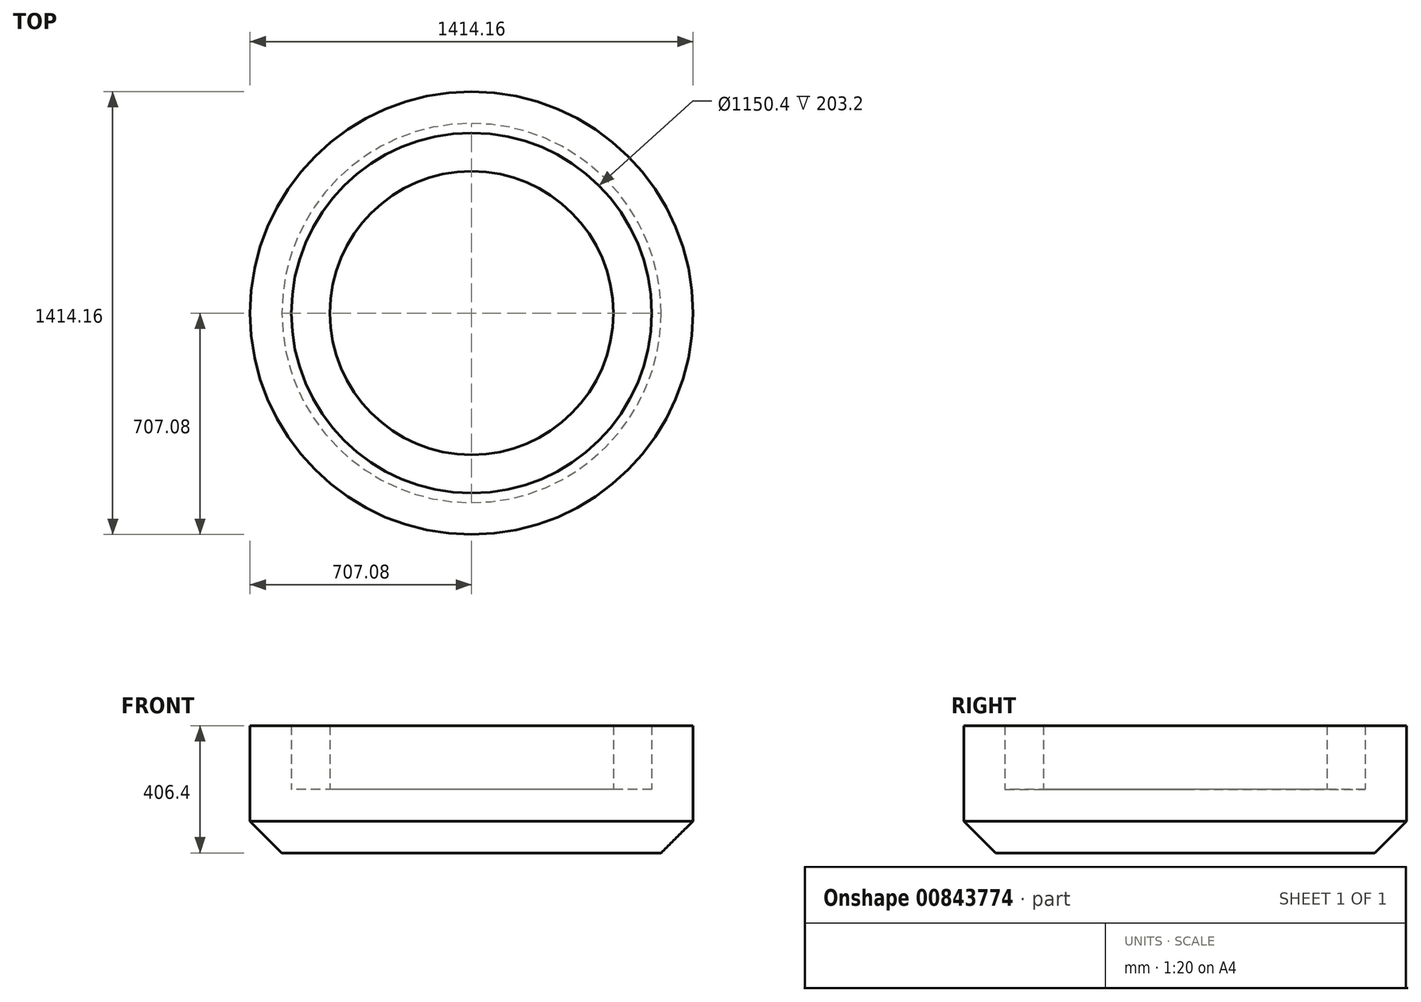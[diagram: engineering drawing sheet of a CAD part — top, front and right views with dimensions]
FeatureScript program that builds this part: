
annotation { "Feature Type Name" : "Feature", "Feature Type Description" : "" }
export const myFeature = defineFeature(function(context is Context, id is Id, definition is map)
    precondition{}
    {
        {
            var Q0;
            Q0=qCreatedBy(makeId("Top.planeOp"),FACE);
            var sketch = newSketch(context, id + "F0", { "sketchPlane" : qUnion([Q0])});
            skCircle(sketch, "E0", {"center": v(0, 0) * mm, "radius": 707.08 * mm});
            skCircle(sketch, "E1", {"center": v(0, 0) * mm, "radius": 575.2 * mm});
            skCircle(sketch, "E2", {"center": v(0, 0) * mm, "radius": 452.54 * mm});
            skSolve(sketch);
        }
        {
            var Q0;
            Q0=makeQuery(id+"F0.imprint","IMPRINT",FACE,{"disambiguationData":[TD([[makeQuery(id+"F0.imprint","IMPRINT",EDGE,{"derivedFrom":sQuery(id+"F0.wireOp",EDGE,"E0")}),1.0]])]});
            var Q1;
            Q1=makeQuery(id+"F0.imprint","IMPRINT",FACE,{"disambiguationData":[TD([[makeQuery(id+"F0.imprint","IMPRINT",EDGE,{"derivedFrom":sQuery(id+"F0.wireOp",EDGE,"bqpiEDL7-e6hC-lYBw-wX8p-t1UnFi6AQx9M")}),1.0]])]});
            var Q2;
            Q2=makeQuery(id+"F0.imprint","IMPRINT",FACE,{"disambiguationData":[TD([[makeQuery(id+"F0.imprint","IMPRINT",EDGE,{"derivedFrom":sQuery(id+"F0.wireOp",EDGE,"XZNxxLQD-RQr5-d4jD-ZKYX-YBIh4HYT3hMv")}),1.0]])]});
            var Q3;
            Q3=makeQuery(id+"F0.imprint","IMPRINT",FACE,{"disambiguationData":[TD([[makeQuery(id+"F0.imprint","IMPRINT",EDGE,{"derivedFrom":sQuery(id+"F0.wireOp",EDGE,"E1")}),1.0]])]});
            var Q4;
            Q4=makeQuery(id+"F0.imprint","IMPRINT",FACE,{"disambiguationData":[TD([[makeQuery(id+"F0.imprint","IMPRINT",EDGE,{"derivedFrom":sQuery(id+"F0.wireOp",EDGE,"E2")}),1.0]])]});
            extrude(context, id + "F1", {"entities" : qUnion([Q0, Q1, Q2, Q3, Q4]), "oppositeDirection" : true, "depth" : 203.2 * mm, "offsetDistance" : 25.4 * mm});
        }
        {
            var Q0;
            Q0=makeQuery(id+"F0.imprint","IMPRINT",FACE,{"disambiguationData":[TD([[makeQuery(id+"F0.imprint","IMPRINT",EDGE,{"derivedFrom":sQuery(id+"F0.wireOp",EDGE,"E0")}),1.0]])]});
            var Q1;
            Q1=makeQuery(id+"F0.imprint","IMPRINT",FACE,{"disambiguationData":[TD([[makeQuery(id+"F0.imprint","IMPRINT",EDGE,{"derivedFrom":sQuery(id+"F0.wireOp",EDGE,"XZNxxLQD-RQr5-d4jD-ZKYX-YBIh4HYT3hMv")}),1.0]])]});
            var Q2;
            Q2=makeQuery(id+"F0.imprint","IMPRINT",FACE,{"disambiguationData":[TD([[makeQuery(id+"F0.imprint","IMPRINT",EDGE,{"derivedFrom":sQuery(id+"F0.wireOp",EDGE,"E2")}),1.0]])]});
            extrude(context, id + "F2", {"entities" : qUnion([Q0, Q1, Q2]), "operationType" : NewBodyOperationType.ADD, "depth" : 203.2 * mm, "offsetDistance" : 25.4 * mm});
        }
        {
            var Q0;
            Q0=makeQuery(id+"F1.opExtrude","CAP_EDGE",EDGE,{"disambiguationData":[OSD([sQuery(id+"F0.wireOp",EDGE,"E0")])],"isStart":false});
            chamfer(context, id + "F3", {"entities" : qUnion([Q0]), "width" : 101.6 * mm, "tangentPropagation" : true});
        }
    });
